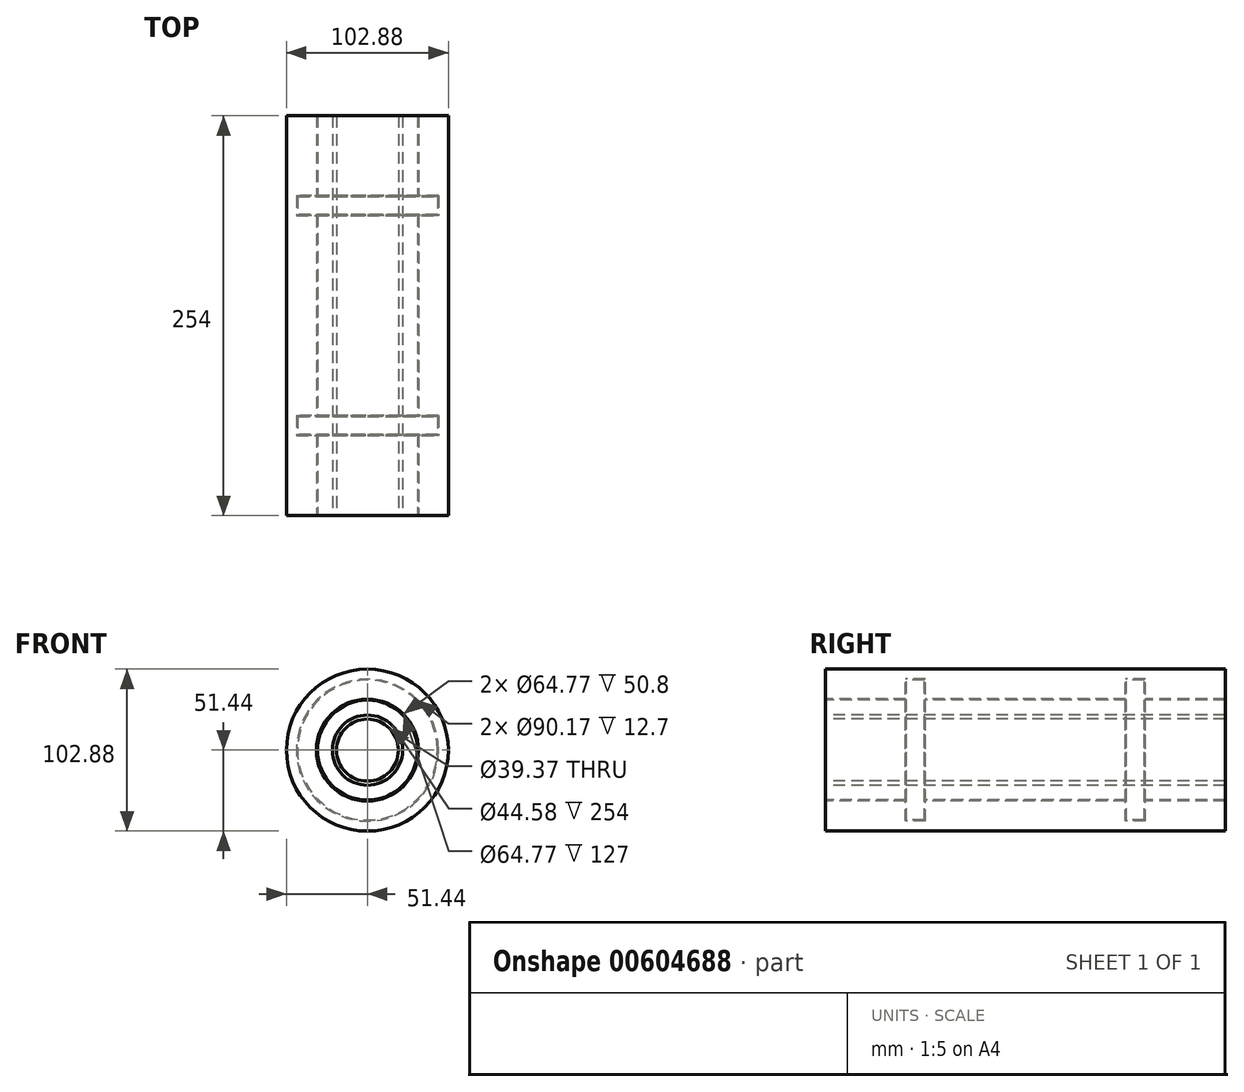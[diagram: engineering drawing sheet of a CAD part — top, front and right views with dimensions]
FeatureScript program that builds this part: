
annotation { "Feature Type Name" : "Feature", "Feature Type Description" : "" }
export const myFeature = defineFeature(function(context is Context, id is Id, definition is map)
    precondition{}
    {
        {
            var Q0;
            Q0=qCreatedBy(makeId("Top.planeOp"),FACE);
            var sketch = newSketch(context, id + "F0", { "sketchPlane" : qUnion([Q0])});
            skLineSegment(sketch, "E0", {"start": v(0, 0) * mm, "end": v(0, 254) * mm, "construction": true});
            skLineSegment(sketch, "E1", {"start": v(0, 254) * mm, "end": v(32.39, 254) * mm, "construction": true});
            skLineSegment(sketch, "E2", {"start": v(32.39, 254) * mm, "end": v(51.43, 254) * mm});
            skLineSegment(sketch, "E3", {"start": v(51.43, 254) * mm, "end": v(51.44, 0) * mm});
            skLineSegment(sketch, "E4", {"start": v(51.44, 0) * mm, "end": v(32.39, 0) * mm});
            skLineSegment(sketch, "E5", {"start": v(32.39, 0) * mm, "end": v(32.39, 50.8) * mm});
            skLineSegment(sketch, "E6", {"start": v(32.39, 63.5) * mm, "end": v(45.09, 63.5) * mm});
            skLineSegment(sketch, "E7", {"start": v(45.09, 50.8) * mm, "end": v(45.09, 63.5) * mm});
            skLineSegment(sketch, "E8", {"start": v(45.09, 50.8) * mm, "end": v(32.39, 50.8) * mm});
            skLineSegment(sketch, "E9", {"start": v(32.39, 63.5) * mm, "end": v(32.39, 190.5) * mm});
            skLineSegment(sketch, "E10", {"start": v(0, 127) * mm, "end": v(51.44, 127) * mm, "construction": true});
            skLineSegment(sketch, "E11.MirrorCS", {"start": v(32.39, 190.5) * mm, "end": v(45.09, 190.5) * mm});
            skLineSegment(sketch, "E12.MirrorCS", {"start": v(45.09, 203.2) * mm, "end": v(45.09, 190.5) * mm});
            skLineSegment(sketch, "E13.MirrorCS", {"start": v(45.09, 203.2) * mm, "end": v(32.39, 203.2) * mm});
            skLineSegment(sketch, "E14.trimOffspring", {"start": v(32.39, 203.2) * mm, "end": v(32.39, 254) * mm});
            skSolve(sketch);
        }
        {
            var Q0;
            Q0 = qSketchRegion(id + "F0", true);
            var Q1;
            Q1=sQuery(id+"F0.wireOp",EDGE,"E0");
            revolve(context, id + "F1", {"entities" : qUnion([Q0]), "axis" : qUnion([Q1]), "revolveType" : RevolveType.FULL});
        }
        {
            var Q0;
            Q0=qCreatedBy(makeId("Top.planeOp"),FACE);
            var sketch = newSketch(context, id + "F2", { "sketchPlane" : qUnion([Q0])});
            skLineSegment(sketch, "E15", {"start": v(0, 0) * mm, "end": v(0, 254) * mm, "construction": true});
            skLineSegment(sketch, "E16", {"start": v(0, 254) * mm, "end": v(22.29, 254) * mm, "construction": true});
            skLineSegment(sketch, "E17", {"start": v(22.29, 254) * mm, "end": v(31.75, 254) * mm});
            skLineSegment(sketch, "E18", {"start": v(31.75, 254) * mm, "end": v(31.75, 202.56) * mm});
            skLineSegment(sketch, "E19", {"start": v(31.75, 202.56) * mm, "end": v(44.45, 202.56) * mm});
            skLineSegment(sketch, "E20", {"start": v(44.45, 202.56) * mm, "end": v(44.45, 191.13) * mm});
            skLineSegment(sketch, "E21", {"start": v(44.45, 191.13) * mm, "end": v(31.75, 191.13) * mm});
            skLineSegment(sketch, "E22", {"start": v(31.75, 191.13) * mm, "end": v(31.75, 127) * mm});
            skLineSegment(sketch, "E23", {"start": v(22.29, 254) * mm, "end": v(22.29, 127) * mm});
            skPoint(sketch, "E23.endSnap0", {"position": v(0, 127) * mm});
            skLineSegment(sketch, "E24.MirrorCS", {"start": v(22.29, 0) * mm, "end": v(22.29, 127) * mm});
            skLineSegment(sketch, "E25.MirrorCS", {"start": v(31.75, 62.87) * mm, "end": v(31.75, 127) * mm});
            skLineSegment(sketch, "E26.MirrorCS", {"start": v(44.45, 62.87) * mm, "end": v(31.75, 62.87) * mm});
            skLineSegment(sketch, "E27.MirrorCS", {"start": v(44.45, 51.44) * mm, "end": v(44.45, 62.87) * mm});
            skLineSegment(sketch, "E28.MirrorCS", {"start": v(31.75, 51.44) * mm, "end": v(44.45, 51.44) * mm});
            skLineSegment(sketch, "E29.MirrorCS", {"start": v(31.75, 0) * mm, "end": v(31.75, 51.44) * mm});
            skLineSegment(sketch, "E30.MirrorCS", {"start": v(22.29, 0) * mm, "end": v(31.75, 0) * mm});
            skSolve(sketch);
        }
        {
            var Q0;
            Q0 = qSketchRegion(id + "F2", true);
            var Q1;
            Q1=sQuery(id+"F2.wireOp",EDGE,"E15");
            revolve(context, id + "F3", {"entities" : qUnion([Q0]), "axis" : qUnion([Q1]), "revolveType" : RevolveType.FULL});
        }
        {
            var Q0;
            Q0=qCreatedBy(makeId("Top.planeOp"),FACE);
            var sketch = newSketch(context, id + "F4", { "sketchPlane" : qUnion([Q0])});
            skLineSegment(sketch, "E31", {"start": v(0, 0) * mm, "end": v(0, 254) * mm, "construction": true});
            skLineSegment(sketch, "E32", {"start": v(0, 254) * mm, "end": v(19.69, 254) * mm, "construction": true});
            skLineSegment(sketch, "E33", {"start": v(19.69, 254) * mm, "end": v(31.75, 254) * mm});
            skLineSegment(sketch, "E34", {"start": v(31.75, 254) * mm, "end": v(31.75, 202.56) * mm});
            skLineSegment(sketch, "E35", {"start": v(31.75, 202.56) * mm, "end": v(44.45, 202.56) * mm});
            skLineSegment(sketch, "E36", {"start": v(44.45, 202.56) * mm, "end": v(44.45, 191.13) * mm});
            skLineSegment(sketch, "E37", {"start": v(44.45, 191.13) * mm, "end": v(31.75, 191.13) * mm});
            skLineSegment(sketch, "E38", {"start": v(0, 127) * mm, "end": v(31.75, 127) * mm, "construction": true});
            skLineSegment(sketch, "E39", {"start": v(31.75, 127) * mm, "end": v(31.75, 191.13) * mm});
            skLineSegment(sketch, "E40", {"start": v(19.69, 254) * mm, "end": v(19.69, 127) * mm});
            skLineSegment(sketch, "E41.MirrorCS", {"start": v(19.69, 0) * mm, "end": v(19.69, 127) * mm});
            skLineSegment(sketch, "E42.MirrorCS", {"start": v(31.75, 127) * mm, "end": v(31.75, 62.87) * mm});
            skLineSegment(sketch, "E43.MirrorCS", {"start": v(44.45, 62.87) * mm, "end": v(31.75, 62.87) * mm});
            skLineSegment(sketch, "E44.MirrorCS", {"start": v(44.45, 51.44) * mm, "end": v(44.45, 62.87) * mm});
            skLineSegment(sketch, "E45.MirrorCS", {"start": v(31.75, 51.44) * mm, "end": v(44.45, 51.44) * mm});
            skLineSegment(sketch, "E46.MirrorCS", {"start": v(31.75, 0) * mm, "end": v(31.75, 51.44) * mm});
            skLineSegment(sketch, "E47.MirrorCS", {"start": v(19.69, 0) * mm, "end": v(31.75, 0) * mm});
            skSolve(sketch);
        }
        {
            var Q0;
            Q0 = qSketchRegion(id + "F4", true);
            var Q1;
            Q1=sQuery(id+"F4.wireOp",EDGE,"E31");
            revolve(context, id + "F5", {"entities" : qUnion([Q0]), "axis" : qUnion([Q1]), "revolveType" : RevolveType.FULL});
        }
    });
